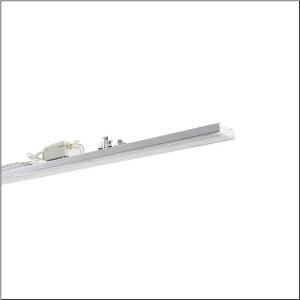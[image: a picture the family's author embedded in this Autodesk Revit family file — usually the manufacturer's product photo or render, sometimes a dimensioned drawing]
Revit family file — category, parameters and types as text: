
# Revit family: licross_r__21_recessed_mo_52tl10dn4axg_1c07
name_source: partatom
category: Lighting Fixtures
units: mm (PartAtom-declared; Revit-internal decimal feet)

## family parameters
Cut with Voids When Loaded = No
Host = Face
Light Source = No
Part Type = Normal
Room Calculation Point = No
Round Connector Dimension = Use Diameter
Shared = No

## types (1)
- --- (1 x LED, 10000 lm, 58 W, 4000K)
    Apparent Load = 58 VA
    CIE Flux Codes = 50 81 96 100 100
    Color Rendering = 80
    Color Temperature = 4000K
    Default Elevation = 1800 mm
    Description = Licross® 21 Recessed MO, luminaire insert, of sheet steel, galvanised, coil coated, white, length: 1.500mm, width: 66mm, height: 67mm, LED rated luminous flux: 10.000lm, light colour: 840, control gear: DALI 2, with plug, 5-pole, with phase selection, mains connection: 220..240V, AC, 50/60Hz, rated input power: 58W, halogen-free wiring, primary optical cover: cover, of PMMA, light emission: direct distribution, primary light characteristic: symmetric, protection rating (complete): IP40, insulation class (complete): insulation class I (protective earthing), certification: CE, ENEC, VDE, UKCA, protection symbol: D if used in an environment without relevant dust loads with corresponding accessories, impact resistance: IK06, permissible ambient temperature for indoor applications: -25..+35°C, corresponds to IFS (International Featured Standards) requirements for safety and quality in the food industry, reducing of maximum allowable ambient temperature of 5°C with ceiling mounting, LABS conformity tested according to VDMA 24364:2018-05, packaging unit: 1 piece
    Height = 58 mm
    Lamp = 1 x LED
    Lamp Light Flux = 10000 lm
    Lamp Power = 58 W
    Lamp count = 1
    Length = 1500 mm
    Luminous efficacy = 172 lm/W
    Manufacturer = Siteco
    ModVariant = No
    Model = 52TL10DN4AXG
    Mounting Place = Ceiling
    Mounting Type = Pendant
    Number of Poles = 1
    OnlyDefault = Yes
    Power Factor = 1
    Product Name = Licross® 21 Recessed MO
    Product group = luminaire insert
    ProductGroupID = 901
    Protection Class = Protection class I
    Protection Degree = IP 40
    RLX_Detail_Level = 1
    RLX_Emergency_Light_Flux = 0 lm
    RLX_Emergency_Type = 0
    RLX_Emergency_Type_DB = No
    RlxData = <blob elided: 24325 chars, md5=02d0556f>
    Socket = socket
    Standby Power = 0 W
    System Light Flux = 10000 lm
    System Power = 58 W
    Type Comments = factory setting: luminous flux: 100 % | dim-lin: 254 | 390 mA
    Type Image = l_1296930.jpg
    URL = http://relux.com
    VarID = @adj_059161
    Voltage = 0 V
    Weight = 0.00 kg
    Width = 66 mm

## geometry (parser evidence)
native form markers: Blend x4, Sweep x9
no freeform markers — native parametric forms only
